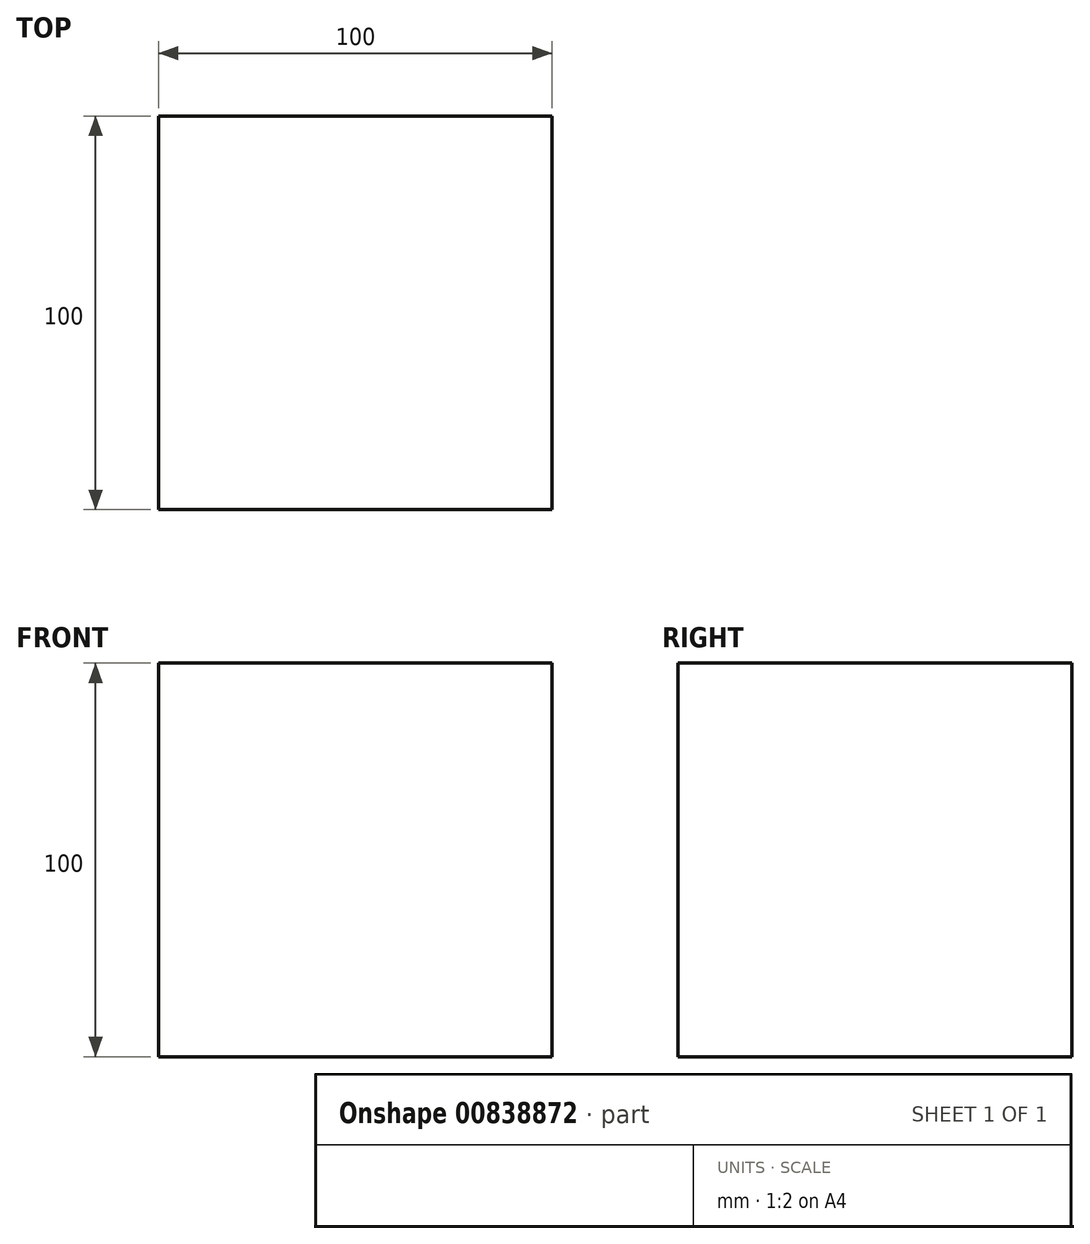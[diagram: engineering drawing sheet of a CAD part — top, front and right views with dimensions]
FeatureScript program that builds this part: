
annotation { "Feature Type Name" : "Feature", "Feature Type Description" : "" }
export const myFeature = defineFeature(function(context is Context, id is Id, definition is map)
    precondition{}
    {
        {
            var Q0;
            Q0=qCreatedBy(makeId("Top.planeOp"),FACE);
            var sketch = newSketch(context, id + "F0", { "sketchPlane" : qUnion([Q0])});
            skLineSegment(sketch, "E0.bottom", {"start": v(-50, 50) * mm, "end": v(50, 50) * mm});
            skLineSegment(sketch, "E0.top", {"start": v(-50, -50) * mm, "end": v(50, -50) * mm});
            skLineSegment(sketch, "E0.left", {"start": v(-50, 50) * mm, "end": v(-50, -50) * mm});
            skLineSegment(sketch, "E0.right", {"start": v(50, 50) * mm, "end": v(50, -50) * mm});
            skPoint(sketch, "E0.middle", {"position": v(0, 0) * mm});
            skSolve(sketch);
        }
        {
            var Q0;
            Q0 = qSketchRegion(id + "F0", true);
            extrude(context, id + "F1", {"entities" : qUnion([Q0]), "depth" : 100 * mm, "offsetDistance" : 25 * mm});
        }
    });
